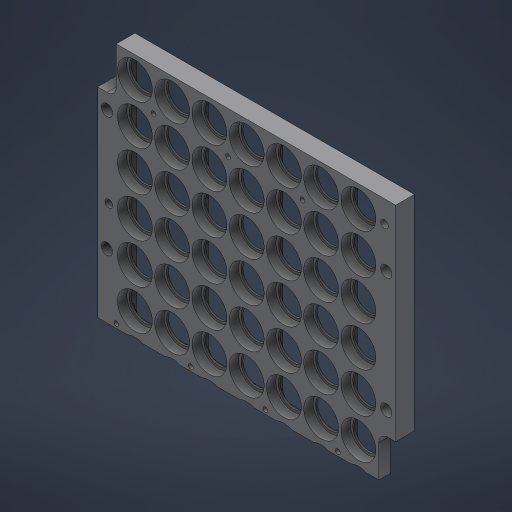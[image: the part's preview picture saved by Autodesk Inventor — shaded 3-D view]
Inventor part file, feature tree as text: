
AUTODESK INVENTOR PART (.ipt)
format: ipt  version: 2024.3 (Build 283343010, 343A)  size: 1,443,328 bytes
history: native  units: mm
features: sketch x7, extrude x6, hole x5, fillet x2, pattern_linear x1, projected_geometry x1
ambient origin geometry x8: Origin, YZ Plane, XZ Plane, XY Plane, X Axis, Y Axis, Z Axis, Center Point
bodies: Volumenkörper1 (feature_tree)
feature tree (22):
  sketch  "Skizze1"  dims[d0=160.0mm d1=260.0mm]
  extrude  "Extrusion1"  Depth=160.0mm
  hole  "Bohrung1"  [1 undecoded]
  pattern_linear  "Rechteckige Anordnung1"  Count1=6 Spacing1=43.0mm
  sketch  "Skizze2"  dims[d2=10.0mm d3=0.0mm d4=18.0mm d5=60.0mm d7=43.0mm d8=70.0mm d10=20.0mm]
  extrude  "Extrusion2"  Depth=70.0mm
  sketch  "Skizze3"  dims[d16=21.5mm d19=70.0mm d21=20.0mm]
  sketch  "Skizze4"  dims[d22=60.0mm d24=43.0mm d69=15.0mm]
  extrude  "Extrusion6"  Depth=60.0mm
  extrude  "Extrusion7"  Depth=70.0mm
  hole  "Bohrung5"  [1 undecoded]
  hole  "Bohrung6"  [1 undecoded]
  extrude  "Extrusion9"  Depth=10.0mm TaperAngle=0.0deg
  hole  "Bohrung7"  [1 undecoded]
  fillet  "Rundung4"  Radius=157.7mm
  sketch  "Skizze9"  dims[d84=5.0mm d85=60.0mm d89=10.0mm d90=0.0mm d101=25.0mm d113=157.7mm d119=8.0mm d121=6.0mm d124=33.25mm d125=64.5mm d126=6.0mm d127=10.75mm d129=7.0mm d130=7.0mm d132=3.0mm d134=10.75mm d135=9.5mm d136=3.0mm d142=6.0mm d143=5.0mm d144=5.0mm d145=4.0mm d146=6.0mm d147=4.0mm d148=2.0mm d149=90.0deg d150=8.0mm d151=20.594885mm d160=8.0mm d162=3.0mm d165=20.0mm d166=5.75mm d169=7.0mm d170=7.0mm d171=3.64mm d172=10.75mm d180=1.8mm d181=1.8mm d182=5.0mm d184=8.95mm d185=8.95mm d186=4.0mm d187=0.0mm d190=40.0mm d191=20.0mm d192=0.0mm d193=0.0mm d195=60.0mm d196=60.0mm d197=4.0mm d198=6.0mm d199=6.0mm d200=5.0mm d201=90.0deg d202=8.0mm d203=20.594885mm d204=4.0mm d205=6.0mm d206=6.0mm d207=5.0mm d208=90.0deg d209=8.0mm d210=20.594885mm d222=37.9mm d223=127.4mm d224=5.0mm d225=30.0mm d227=40.0mm d228=20.0mm d230=129.0mm d233=0.0mm d234=0.0mm d236=5.0mm d237=5.0mm d238=2.4mm d239=0.0mm d240=9.0mm d241=2.5mm d242=6.0mm d243=19.05mm d244=4.775mm d245=90.0deg d246=8.0mm d247=20.594885mm d251=40.0mm d252=107.5mm d254=3.0mm d256=3.0mm d257=6.0mm d258=3.0mm d259=5.0mm d260=40.0mm d261=40.0mm d262=20.0mm d263=0.0mm d264=0.0mm d265=200.0mm d266=300.0mm d267=5.0mm d268=5.0mm d275=5.0mm d276=5.0mm d277=5.0mm d278=8.95mm d280=107.5mm d281=107.5mm d118=0.5mm d120=0.5mm]
  extrude  "Extrusion10"  Depth=8.0mm
  fillet  "Rundung3"  Radius=6.0mm
  hole  "Bohrung3"  [1 undecoded]
  sketch  "Skizze5"  dims[d70=16.0mm d71=6.0mm d72=18.7mm d73=5.0mm d74=90.0deg d75=8.0mm d76=20.594885mm d77=70.0mm d79=20.0mm]
  sketch  "Skizze8"  dims[d80=0.0mm d83=10.0mm]
  projected_geometry  "Projizierte Kontur3"
note: 5 required parameter values undecoded (feature->parameter linkage not recoverable at this tier; creation-order binding heuristic only, values carry confidence <= 0.55)
